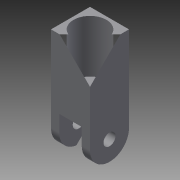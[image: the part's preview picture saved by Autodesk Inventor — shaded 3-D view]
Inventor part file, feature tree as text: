
AUTODESK INVENTOR PART (.ipt)
format: ipt  version: 2014 SP2 (Build 180246200, 246)  size: 130,048 bytes
history: native  units: mm
features: extrude x4, sketch x4, fillet x1
ambient origin geometry x8: Origin, YZ Plane, XZ Plane, XY Plane, X Axis, Y Axis, Z Axis, Center Point
bodies: Solid1 (feature_tree)
feature tree (9):
  extrude  "Extrusion1"  Depth=30.0mm
  extrude  "Extrusion2"  Depth=26.0mm
  fillet  "Fillet1"  Radius=26.0mm
  extrude  "Extrusion3"  Depth=26.0mm
  extrude  "Extrusion5"  Depth=13.0mm
  sketch  "Sketch1"  dims[d0=22.0mm d1=30.0mm]
  sketch  "Sketch2"  dims[d2=15.0mm d3=8.0mm d6=26.0mm d7=0.0mm]
  sketch  "Sketch3"  dims[d8=26.0mm d9=40.0mm]
  sketch  "Sketch4"  dims[d10=8.0mm d11=13.0mm d12=26.0mm d13=0.0mm d14=13.0mm d15=22.0mm d16=35.0mm d17=0.0mm d20=35.0mm d21=0.0mm]
